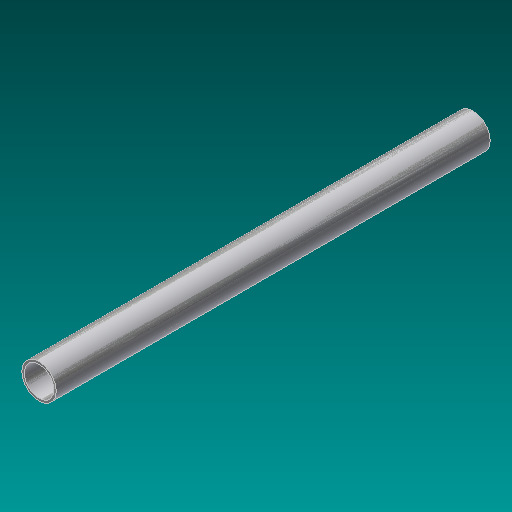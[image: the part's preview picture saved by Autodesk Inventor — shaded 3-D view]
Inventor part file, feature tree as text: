
AUTODESK INVENTOR PART (.ipt)
format: ipt  version: 2017 (Build 210142000, 142)  size: 111,616 bytes
history: native  units: in
note: dims shown in document units (in); Inventor stores cm internally (conversion verified against a paired STEP export)
features: extrude x1, sketch x1
ambient origin geometry x8: Origin, YZ Plane, XZ Plane, XY Plane, X Axis, Y Axis, Z Axis, Center Point
bodies: Solid1 (feature_tree)
feature tree (2):
  extrude  "Extrusion1"  Depth=36.25in
  sketch  "Sketch1"  dims[d0=2.875in d1=2.469in d2=36.25in d3=0.0in]
